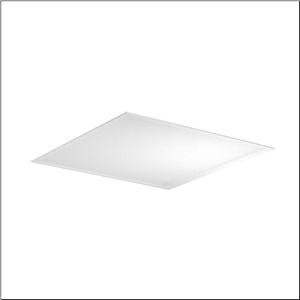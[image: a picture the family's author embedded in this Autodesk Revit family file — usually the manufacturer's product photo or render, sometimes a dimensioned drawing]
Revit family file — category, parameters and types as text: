
# Revit family: apollon_r__31_square_51mp12wd2342_f4b0
name_source: partatom
category: Lighting Fixtures
units: mm (PartAtom-declared; Revit-internal decimal feet)

## family parameters
Cut with Voids When Loaded = No
Host = Face
Light Source = No
Part Type = Normal
Room Calculation Point = No
Round Connector Dimension = Use Diameter
Shared = No

## types (1)
- Apollon® 31 square (1 x LED, 3600 lm, 27.5 W, 3000K)
    Apparent Load = 28 VA
    CIE Flux Codes = 61 87 97 100 100
    Color Rendering = 80
    Color Temperature = 3000K
    Default Elevation = 1800 mm
    Description = Apollon® 31 square, office luminaire, primary optical cover: micro prismatic cover, of PMMA, CAT 2 (L<= 3000cd/m²), light emission: direct distribution, primary light characteristic: symmetric, installation type: lay-in mounting, LED, rated luminous flux: 3.600lm, luminous efficacy: 130lm/W, light colour: 830, colour temperature: 3000K, with terminal, 5-pole, mains connection: 220..240V, AC/DC, 0/50..60Hz, rated input power: 27.5W, housing, of aluminium, traffic white (RAL 9016), module: M600, length: 595mm, width: 595mm, height: 32mm, housing upper side, of sheet steel, galvanised, protection rating (complete): IP20, protection rating (on room side): IP40, insulation class (complete): insulation class II (safety insulation), certification: CE, ENEC, impact resistance: IK03, permissible operating ambient temperature: -20..+40°C, permissible storage temperature: -20..+60°C, packaging unit: 1 piece
    Height = 0 mm  [stored 0 ft]
    Lamp = 1 x LED
    Lamp Light Flux = 3600 lm
    Lamp Power = 27.5 W
    Lamp count = 1
    Length = 595 mm
    Luminous efficacy = 131 lm/W
    Manufacturer = Siteco
    ModVariant = No
    Model = 51MP12WD2342
    Mounting Place = Ceiling
    Mounting Type = Recessed
    Number of Poles = 1
    OnlyDefault = Yes
    Power Factor = 1
    Product Name = Apollon® 31 square
    Product group = office luminaire | ceiling recessed
    ProductGroupID = 401
    Protection Class = Protection class II
    Protection Degree = IP 20
    RLX_Detail_Level = 1
    RLX_Emergency_Light_Flux = 0 lm
    RLX_Emergency_Type = 0
    RLX_Emergency_Type_DB = No
    RlxData = <blob elided: 12497 chars, md5=024e9a77>
    Socket = socket
    Standby Power = 0 W
    System Light Flux = 3600 lm
    System Power = 28 W
    Type Comments = Product without accessories
    Type Image = l_1291035.jpg
    URL = http://relux.com
    VarID = ---
    Voltage = 0 V
    Weight = 0.00 kg
    Width = 595 mm

note: [stored X ft] marks values corroborated as IEEE doubles in the binary element streams (Revit-internal decimal feet)

## geometry (parser evidence)
native form markers: Sweep x11
no freeform markers — native parametric forms only
